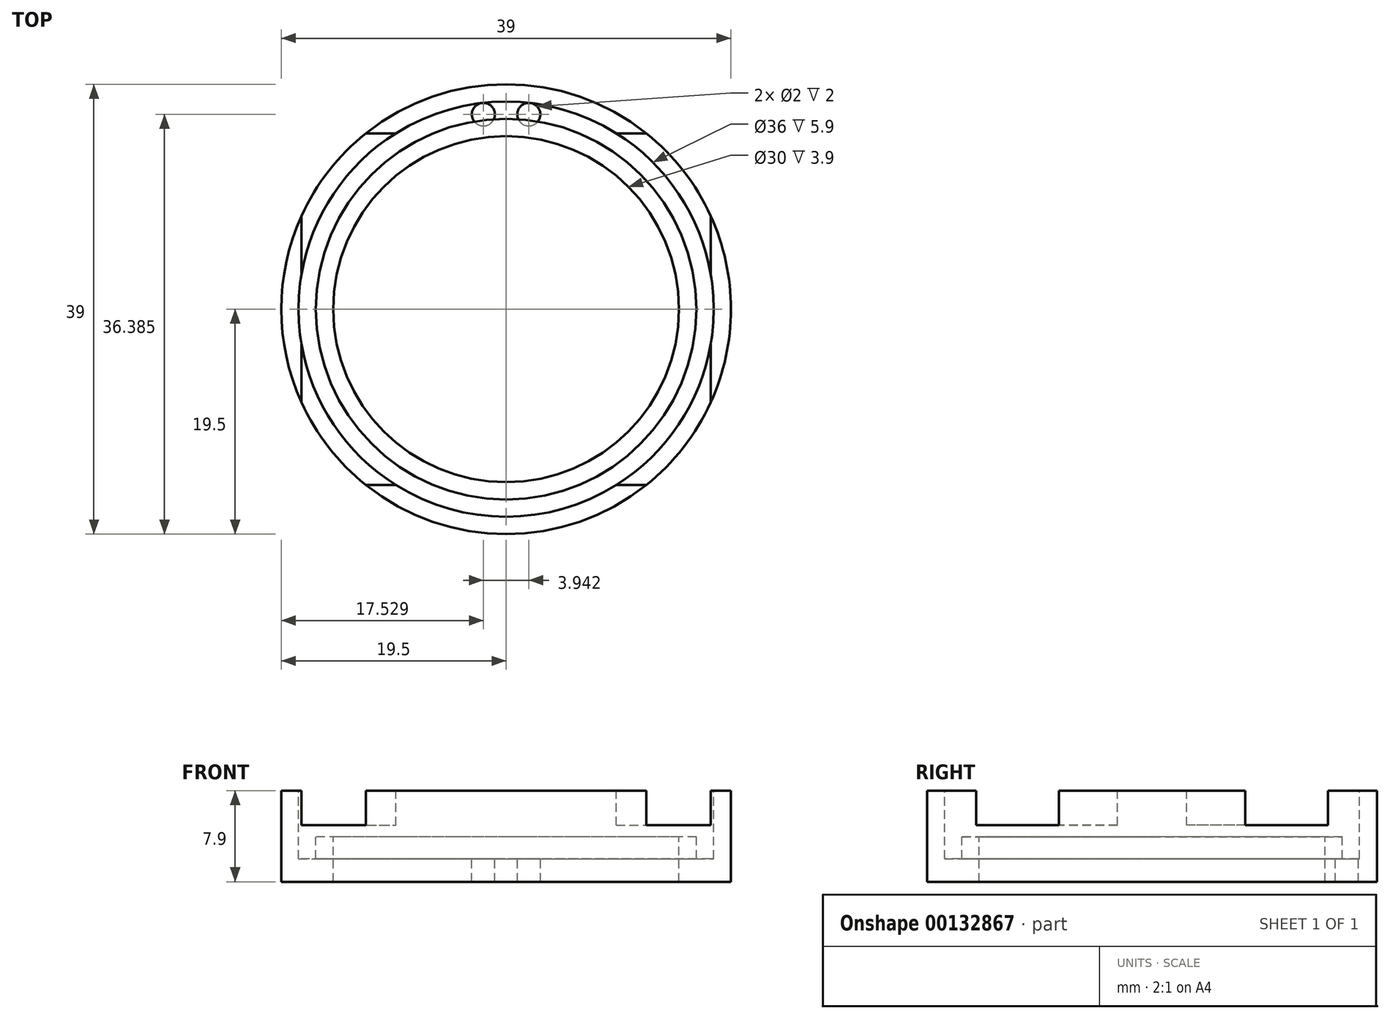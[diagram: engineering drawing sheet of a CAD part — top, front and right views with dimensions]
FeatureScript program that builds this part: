
annotation { "Feature Type Name" : "Feature", "Feature Type Description" : "" }
export const myFeature = defineFeature(function(context is Context, id is Id, definition is map)
    precondition{}
    {
        {
            var Q0;
            Q0=qCreatedBy(makeId("Front.planeOp"),FACE);
            var sketch = newSketch(context, id + "F0", { "sketchPlane" : qUnion([Q0])});
            skLineSegment(sketch, "E0", {"start": v(-16.5, -4) * mm, "end": v(-16.5, -5.9) * mm});
            skLineSegment(sketch, "E1", {"start": v(-16.5, -5.9) * mm, "end": v(-18, -5.9) * mm});
            skLineSegment(sketch, "E2", {"start": v(-18, -5.9) * mm, "end": v(-18, 0) * mm});
            skLineSegment(sketch, "E3", {"start": v(-18, 0) * mm, "end": v(-19.5, 0) * mm});
            skLineSegment(sketch, "E4", {"start": v(-19.5, 0) * mm, "end": v(-19.5, -7.9) * mm});
            skLineSegment(sketch, "E5", {"start": v(-19.5, -7.9) * mm, "end": v(-15, -7.9) * mm});
            skLineSegment(sketch, "E6", {"start": v(-15, -7.9) * mm, "end": v(-15, -4) * mm});
            skLineSegment(sketch, "E7", {"start": v(-15, -4) * mm, "end": v(-16.5, -4) * mm});
            skPoint(sketch, "E8.trimOffspring.end.orphan", {"position": v(0, -12.35) * mm});
            skPoint(sketch, "E8.trimOffspring.start.orphan", {"position": v(0, -1.75) * mm});
            skPoint(sketch, "E9.end.orphan", {"position": v(0, 0) * mm});
            skPoint(sketch, "E9.start.orphan", {"position": v(0, 13.33) * mm});
            skLineSegment(sketch, "E10", {"start": v(0, 5.58) * mm, "end": v(0, -15.25) * mm, "construction": true});
            skSolve(sketch);
        }
        {
            var Q0;
            Q0 = qSketchRegion(id + "F0", true);
            var Q1;
            Q1=sQuery(id+"F0.wireOp",EDGE,"E10");
            revolve(context, id + "F1", {"entities" : qUnion([Q0]), "axis" : qUnion([Q1]), "revolveType" : RevolveType.FULL});
        }
        {
            var Q0;
            Q0=makeQuery(id+"F1.opRevolve","SWEPT_FACE",FACE,{"disambiguationData":[OSD([sQuery(id+"F0.wireOp",EDGE,"E1")])]});
            var sketch = newSketch(context, id + "F2", { "sketchPlane" : qUnion([Q0])});
            skCircle(sketch, "E11", {"center": v(-1.97, 16.89) * mm, "radius": 1 * mm});
            skLineSegment(sketch, "E12", {"start": v(0, 23.28) * mm, "end": v(0, 4.93) * mm, "construction": true});
            skCircle(sketch, "E13.MirrorC", {"center": v(1.97, 16.89) * mm, "radius": 1 * mm});
            skSolve(sketch);
        }
        {
            var Q0;
            Q0 = qSketchRegion(id + "F2", true);
            extrude(context, id + "F3", {"entities" : qUnion([Q0]), "operationType" : NewBodyOperationType.REMOVE, "oppositeDirection" : true, "depth" : 25 * mm});
        }
        {
            var Q0;
            Q0=makeQuery(id+"F1.opRevolve","SWEPT_FACE",FACE,{"disambiguationData":[OSD([sQuery(id+"F0.wireOp",EDGE,"E3")])]});
            var sketch = newSketch(context, id + "F4", { "sketchPlane" : qUnion([Q0])});
            skLineSegment(sketch, "E14.bottom", {"start": v(-17.75, 15.25) * mm, "end": v(17.75, 15.25) * mm});
            skLineSegment(sketch, "E14.top", {"start": v(-17.75, -15.25) * mm, "end": v(17.75, -15.25) * mm});
            skLineSegment(sketch, "E14.left", {"start": v(-17.75, 15.25) * mm, "end": v(-17.75, -15.25) * mm});
            skLineSegment(sketch, "E14.right", {"start": v(17.75, 15.25) * mm, "end": v(17.75, -15.25) * mm});
            skPoint(sketch, "E14.middle", {"position": v(0, 0) * mm});
            skSolve(sketch);
        }
        {
            var Q0;
            Q0 = qSketchRegion(id + "F4", true);
            extrude(context, id + "F5", {"entities" : qUnion([Q0]), "operationType" : NewBodyOperationType.REMOVE, "oppositeDirection" : true, "depth" : 3 * mm});
        }
    });
